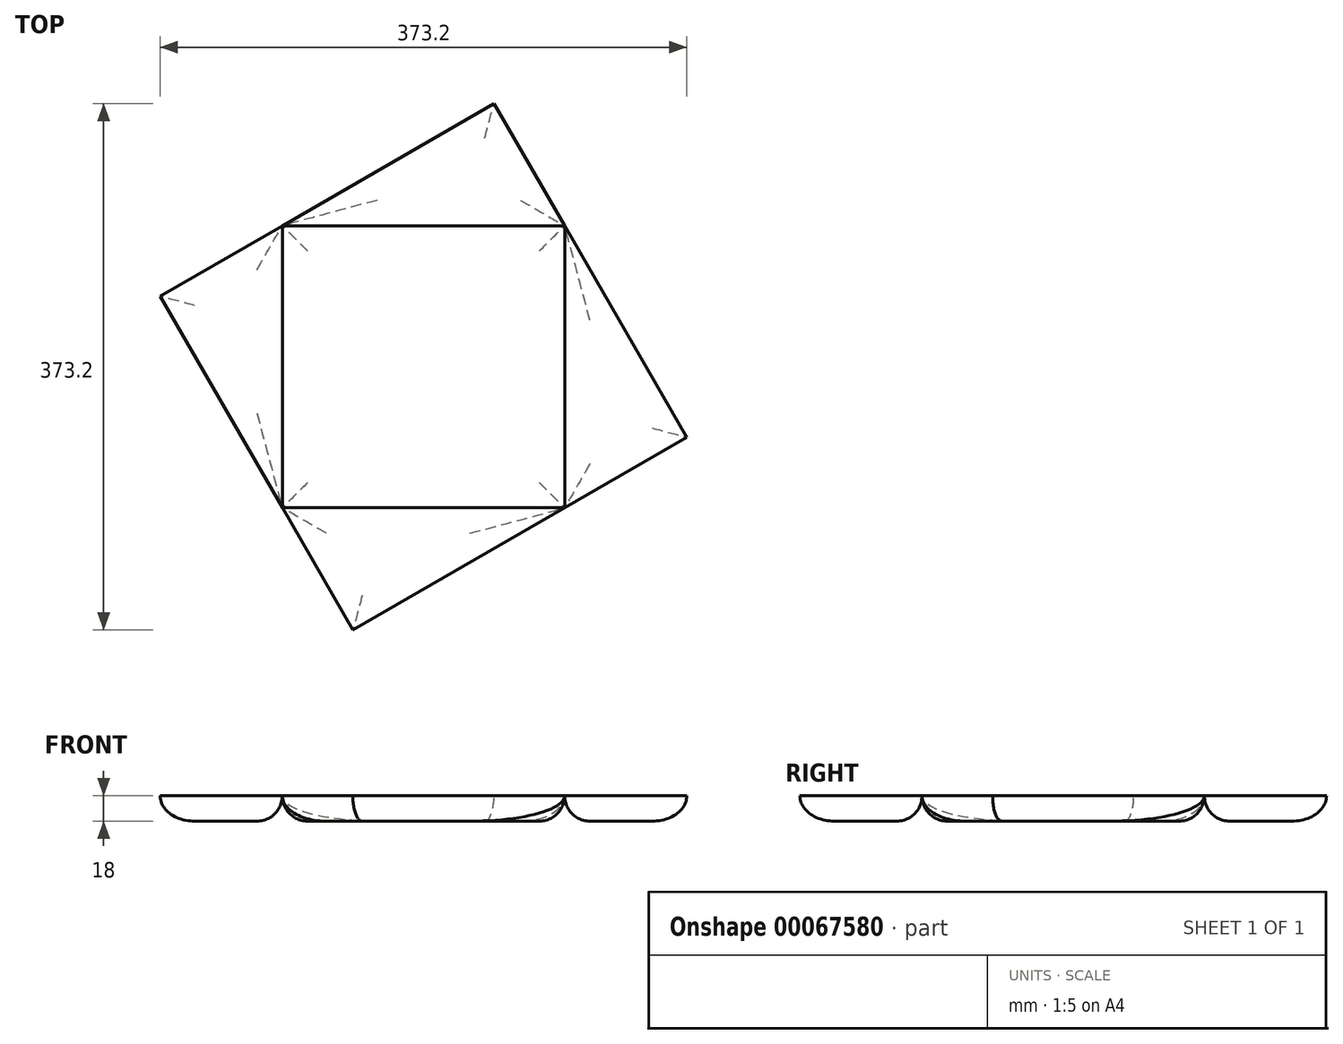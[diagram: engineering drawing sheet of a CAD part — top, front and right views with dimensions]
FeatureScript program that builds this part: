
annotation { "Feature Type Name" : "Feature", "Feature Type Description" : "" }
export const myFeature = defineFeature(function(context is Context, id is Id, definition is map)
    precondition{}
    {
        {
            var Q0;
            Q0=qCreatedBy(makeId("Top.planeOp"),FACE);
            var sketch = newSketch(context, id + "F0", { "sketchPlane" : qUnion([Q0])});
            skLineSegment(sketch, "E0.rect.bottom", {"start": v(100, -100) * mm, "end": v(-100, -100) * mm});
            skLineSegment(sketch, "E0.rect.top", {"start": v(100, 100) * mm, "end": v(-100, 100) * mm});
            skLineSegment(sketch, "E0.rect.left", {"start": v(100, -100) * mm, "end": v(100, 100) * mm});
            skLineSegment(sketch, "E0.rect.right", {"start": v(-100, -100) * mm, "end": v(-100, 100) * mm});
            skPoint(sketch, "E0.rect.middle", {"position": v(0, 0) * mm});
            skLineSegment(sketch, "E1", {"start": v(100, 100) * mm, "end": v(186.6, -50) * mm});
            skLineSegment(sketch, "E2", {"start": v(186.6, -50) * mm, "end": v(100, -100) * mm});
            skLineSegment(sketch, "E3.1.0", {"start": v(50, 186.6) * mm, "end": v(100, 100) * mm});
            skLineSegment(sketch, "E3.1.1", {"start": v(-100, 100) * mm, "end": v(50, 186.6) * mm});
            skLineSegment(sketch, "E3.2.0", {"start": v(-186.6, 50) * mm, "end": v(-100, 100) * mm});
            skLineSegment(sketch, "E3.2.1", {"start": v(-100, -100) * mm, "end": v(-186.6, 50) * mm});
            skLineSegment(sketch, "E3.3.0", {"start": v(-50, -186.6) * mm, "end": v(-100, -100) * mm});
            skLineSegment(sketch, "E3.3.1", {"start": v(100, -100) * mm, "end": v(-50, -186.6) * mm});
            skSolve(sketch);
        }
        {
            var Q0;
            Q0=makeQuery(id+"F0.imprint","IMPRINT",FACE,{"disambiguationData":[TD([[makeQuery(id+"F0.imprint","IMPRINT",EDGE,{"derivedFrom":sQuery(id+"F0.wireOp",EDGE,"E0.rect.bottom")}),-1.0]])]});
            extrude(context, id + "F1", {"entities" : qUnion([Q0]), "oppositeDirection" : true, "depth" : 18 * mm});
        }
        {
            var Q0;
            Q0=makeQuery(id+"F0.imprint","IMPRINT",FACE,{"disambiguationData":[TD([[makeQuery(id+"F0.imprint","IMPRINT",EDGE,{"derivedFrom":sQuery(id+"F0.wireOp",EDGE,"E0.rect.right")}),1.0]])]});
            var Q1;
            Q1=makeQuery(id+"F0.imprint","IMPRINT",FACE,{"disambiguationData":[TD([[makeQuery(id+"F0.imprint","IMPRINT",EDGE,{"derivedFrom":sQuery(id+"F0.wireOp",EDGE,"E0.rect.top")}),-1.0]])]});
            var Q2;
            Q2=makeQuery(id+"F0.imprint","IMPRINT",FACE,{"disambiguationData":[TD([[makeQuery(id+"F0.imprint","IMPRINT",EDGE,{"derivedFrom":sQuery(id+"F0.wireOp",EDGE,"E0.rect.left")}),-1.0]])]});
            var Q3;
            Q3=makeQuery(id+"F0.imprint","IMPRINT",FACE,{"disambiguationData":[TD([[makeQuery(id+"F0.imprint","IMPRINT",EDGE,{"derivedFrom":sQuery(id+"F0.wireOp",EDGE,"E0.rect.bottom")}),1.0]])]});
            extrude(context, id + "F2", {"entities" : qUnion([Q0, Q1, Q2, Q3]), "oppositeDirection" : true, "depth" : 18 * mm});
        }
        {
            var Q0;
            Q0=makeQuery(id+"F1.opExtrude","CAP_FACE",FACE,{"disambiguationData":[OSD([sQuery(id+"F0.wireOp",EDGE,"E0.rect.bottom"),sQuery(id+"F0.wireOp",EDGE,"E0.rect.top"),sQuery(id+"F0.wireOp",EDGE,"E0.rect.left"),sQuery(id+"F0.wireOp",EDGE,"E0.rect.right")])],"isStart":false});
            var Q1;
            Q1=makeQuery(id+"F2.opExtrude","CAP_FACE",FACE,{"disambiguationData":[OSD([sQuery(id+"F0.wireOp",EDGE,"E0.rect.top"),sQuery(id+"F0.wireOp",EDGE,"E3.1.0"),sQuery(id+"F0.wireOp",EDGE,"E3.1.1")])],"isStart":false});
            var Q2;
            Q2=makeQuery(id+"F2.opExtrude","CAP_FACE",FACE,{"disambiguationData":[OSD([sQuery(id+"F0.wireOp",EDGE,"E0.rect.left"),sQuery(id+"F0.wireOp",EDGE,"E1"),sQuery(id+"F0.wireOp",EDGE,"E2")])],"isStart":false});
            var Q3;
            Q3=makeQuery(id+"F2.opExtrude","CAP_FACE",FACE,{"disambiguationData":[OSD([sQuery(id+"F0.wireOp",EDGE,"E0.rect.bottom"),sQuery(id+"F0.wireOp",EDGE,"E3.3.0"),sQuery(id+"F0.wireOp",EDGE,"E3.3.1")])],"isStart":false});
            var Q4;
            Q4=makeQuery(id+"F2.opExtrude","CAP_FACE",FACE,{"disambiguationData":[OSD([sQuery(id+"F0.wireOp",EDGE,"E0.rect.right"),sQuery(id+"F0.wireOp",EDGE,"E3.2.0"),sQuery(id+"F0.wireOp",EDGE,"E3.2.1")])],"isStart":false});
            fillet(context, id + "F3", {"entities" : qUnion([Q0, Q1, Q2, Q3, Q4]), "radius" : 18 * mm, "tangentPropagation" : true, "allowEdgeOverflow" : false});
        }
    });
